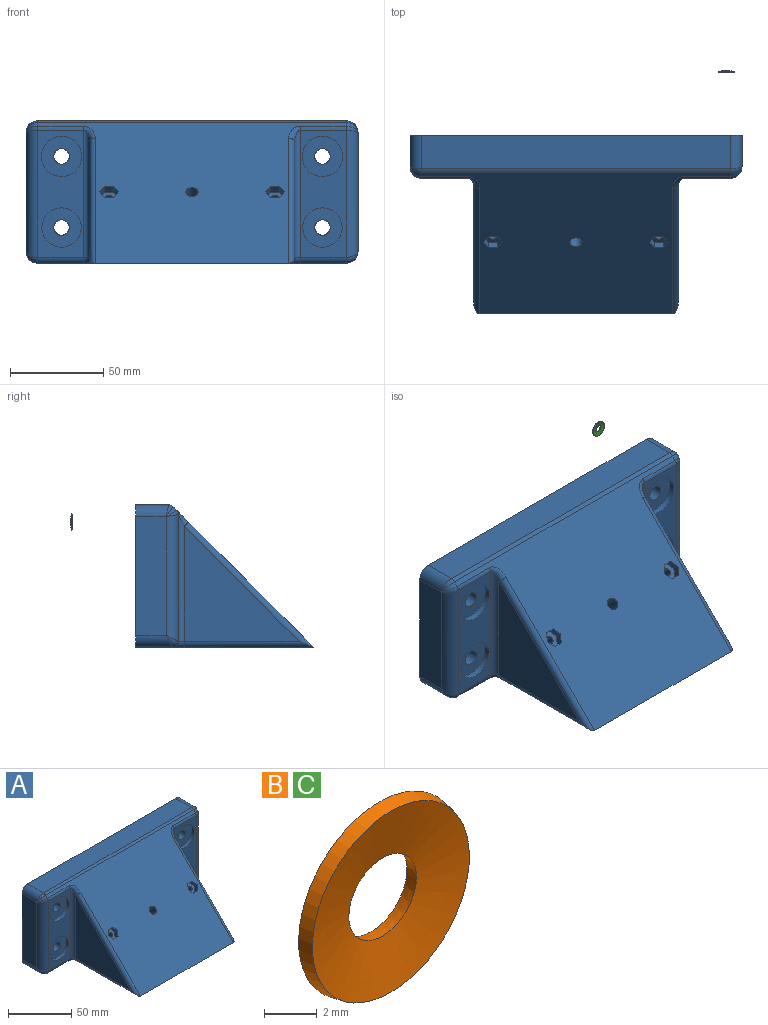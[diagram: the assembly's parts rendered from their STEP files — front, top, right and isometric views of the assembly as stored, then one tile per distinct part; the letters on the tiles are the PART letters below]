
ASSEMBLY  parts=3 mates=1
PART A: 74 faces, bbox 177.8x95.3x89.7 mm
  f0: cylinder r=4.13mm len=19.69mm, axis (0,1,0), area 510.5mm2, adj f10,f60
  f1: cylinder r=4.13mm len=19.69mm, axis (0,1,0), area 510.5mm2, adj f10,f63
  f2: cylinder r=4.13mm len=19.69mm, axis (0,1,0), area 510.5mm2, adj f10,f64
  f3: cylinder r=4.13mm len=19.69mm, axis (0,1,0), area 510.5mm2, adj f10,f67
  f4: plane 165.1x75.27mm, normal (0,-0.71,0.71), area 11064.4mm2, adj f7,f12,f21,f22,f23,f26,f28,f30
  f5: cylinder r=1.98mm len=9.26mm, axis (0,-0.71,0.71), area 113.8mm2, adj f39,f68
  f6: cylinder r=1.98mm len=9.26mm, axis (0,-0.71,0.71), area 113.8mm2, adj f38,f70
  f7: plane 165.1x95.25mm, normal (0,0,-1), area 10510.8mm2, adj f4,f10,f17,f18,f19,f24,f27,f29
  f8: plane 63.5x16.51mm, normal (1,0,0), area 1048.4mm2, adj f10,f53,f55,f57,f59
  f9: plane 63.5x16.51mm, normal (-1,0,0), area 1048.4mm2, adj f10,f46,f48,f50,f52
  f10: plane 177.8x76.2mm, normal (0,1,0), area 13299.7mm2, adj f0,f1,f2,f3,f7,f8,f9,f11
  f11: plane 165.1x17.74mm, normal (0,0,1), area 2928mm2, adj f10,f31,f46,f53
  f12: cylinder r=3.28mm len=17.54mm, axis (0,-0.71,0.71), area 375.9mm2, adj f4,f72
  f13: plane 67.9x24.38mm, normal (0,-1,0), area 939.9mm2, adj f24,f25,f26,f50,f65,f66
  f14: plane 61.55x61.55mm, normal (-1,0,0), area 1894.2mm2, adj f25,f29,f30
  f15: plane 61.55x61.55mm, normal (1,0,0), area 1894.2mm2, adj f19,f20,f21
  f16: plane 67.9x24.38mm, normal (0,-1,0), area 939.9mm2, adj f17,f20,f23,f57,f61,f62
  f17: cylinder r=3.17mm len=24.38mm, axis (-1,0,0), area 121.6mm2, adj f7,f16,f18,f58
  f18: torus R=6.35mm, axis (0,0,-1), area 33.9mm2, adj f7,f17,f19,f20
  f19: cylinder r=3.17mm len=69.22mm, axis (0,-1,0), area 331.3mm2, adj f7,f15,f18,f21
  f20: cylinder r=3.17mm len=67.9mm, axis (0,0,1), area 327.1mm2, adj f15,f16,f18,f22
  f21: cylinder r=3.17mm len=69.22mm, axis (0,-0.71,-0.71), area 458.5mm2, adj f4,f15,f19,f22
  f22: bspline ~9.7x7.45mm, area 35.1mm2, adj f4,f20,f21,f23
  f23: cylinder r=3.17mm len=24.38mm, axis (-1,0,0), area 60.8mm2, adj f4,f16,f22,f56
  f24: cylinder r=3.17mm len=24.38mm, axis (-1,0,0), area 121.6mm2, adj f7,f13,f27,f51
  f25: cylinder r=3.17mm len=67.9mm, axis (0,0,1), area 327.1mm2, adj f13,f14,f27,f28
  f26: cylinder r=3.17mm len=24.38mm, axis (-1,0,0), area 60.8mm2, adj f4,f13,f28,f49
  f27: torus R=6.35mm, axis (0,0,-1), area 33.9mm2, adj f7,f24,f25,f29
  f28: bspline ~9.7x7.45mm, area 35.1mm2, adj f4,f25,f26,f30
  f29: cylinder r=3.17mm len=69.22mm, axis (0,1,0), area 331.3mm2, adj f7,f14,f27,f30
  f30: cylinder r=3.17mm len=69.22mm, axis (0,0.71,0.71), area 458.5mm2, adj f4,f14,f28,f29
  f31: cylinder r=3.17mm len=165.1mm, axis (-1,0,0), area 411.7mm2, adj f4,f11,f47,f54
  f32: plane 4.99x3.09mm, normal (0,0.71,0.71), area 21.8mm2, adj f4,f33,f37,f38
  f33: plane 6.14x6.14mm, normal (-0.87,0.35,0.35), area 21.8mm2, adj f4,f32,f34,f38
  f34: plane 6.14x6.14mm, normal (-0.87,-0.35,-0.35), area 21.8mm2, adj f4,f33,f35,f38
  f35: plane 4.99x3.09mm, normal (0,-0.71,-0.71), area 21.8mm2, adj f4,f34,f36,f38
  f36: plane 6.14x6.14mm, normal (0.87,-0.35,-0.35), area 21.8mm2, adj f4,f35,f37,f38
  f37: plane 6.14x6.14mm, normal (0.87,0.35,0.35), area 21.8mm2, adj f4,f32,f36,f38
  f38: plane 9.97x6.11mm, normal (0,-0.71,0.71), area 52.2mm2, adj f6,f32,f33,f34,f35,f36,f37
  f39: plane 9.97x6.11mm, normal (0,-0.71,0.71), area 52.2mm2, adj f5,f40,f41,f42,f43,f44,f45
  f40: plane 6.14x6.14mm, normal (0.87,-0.35,-0.35), area 21.8mm2, adj f4,f39,f41,f45
  f41: plane 6.14x6.14mm, normal (0.87,0.35,0.35), area 21.8mm2, adj f4,f39,f40,f42
  f42: plane 4.99x3.09mm, normal (0,0.71,0.71), area 21.8mm2, adj f4,f39,f41,f43
  f43: plane 6.14x6.14mm, normal (-0.87,0.35,0.35), area 21.8mm2, adj f4,f39,f42,f44
  f44: plane 6.14x6.14mm, normal (-0.87,-0.35,-0.35), area 21.8mm2, adj f4,f39,f43,f45
  f45: plane 4.99x3.09mm, normal (0,-0.71,-0.71), area 21.8mm2, adj f4,f39,f40,f44
  f46: cylinder r=6.35mm len=17.74mm, axis (0,-1,0), area 172.1mm2, adj f9,f10,f11,f47
  f47: bspline ~7.25x6.35mm, area 16mm2, adj f31,f46,f48
  f48: cylinder r=6.35mm len=6.44mm, axis (0,-0.71,-0.71), area 18mm2, adj f4,f9,f47,f49
  f49: bspline ~7.25x6.35mm, area 16mm2, adj f26,f48,f50
  f50: cylinder r=6.35mm len=67.9mm, axis (0,0,-1), area 661mm2, adj f9,f13,f49,f51
  f51: bspline ~7.58x6.35mm, area 33.3mm2, adj f24,f50,f52
  f52: cylinder r=6.35mm len=19.69mm, axis (0,1,0), area 184.8mm2, adj f7,f9,f10,f51
  f53: cylinder r=6.35mm len=17.74mm, axis (0,1,0), area 172.1mm2, adj f8,f10,f11,f54
  f54: bspline ~7.25x6.35mm, area 16mm2, adj f31,f53,f55
  f55: cylinder r=6.35mm len=6.44mm, axis (0,0.71,0.71), area 18mm2, adj f4,f8,f54,f56
  f56: bspline ~6.58x6.35mm, area 16mm2, adj f23,f55,f57
  f57: cylinder r=6.35mm len=67.9mm, axis (0,0,-1), area 661mm2, adj f8,f16,f56,f58
  f58: bspline ~7.58x6.35mm, area 33.3mm2, adj f17,f57,f59
  f59: cylinder r=6.35mm len=19.69mm, axis (0,-1,0), area 184.8mm2, adj f7,f8,f10,f58
  f60: plane 21.59x21.59mm, normal (0,-1,0), area 312.6mm2, adj f0,f61
  f61: cylinder r=10.79mm len=21.59mm, axis (0,-1,0), area 215.4mm2, adj f16,f60
  f62: cylinder r=10.54mm len=21.08mm, axis (0,-1,0), area 210.3mm2, adj f16,f63
  f63: plane 21.08x21.08mm, normal (0,-1,0), area 295.5mm2, adj f1,f62
  f64: plane 21.08x21.08mm, normal (0,-1,0), area 295.5mm2, adj f2,f65
  f65: cylinder r=10.54mm len=21.08mm, axis (0,-1,0), area 210.3mm2, adj f13,f64
  f66: cylinder r=10.79mm len=21.59mm, axis (0,-1,0), area 215.4mm2, adj f13,f67
  f67: plane 21.59x21.59mm, normal (0,-1,0), area 312.6mm2, adj f3,f66
  f68: plane 9.14x6.47mm, normal (0,0.71,-0.71), area 53.3mm2, adj f5,f69
  f69: cylinder r=4.57mm len=38.26mm, axis (0,0.71,-0.71), area 1160.2mm2, adj f7,f68
  f70: plane 9.14x6.47mm, normal (0,0.71,-0.71), area 53.3mm2, adj f6,f71
  f71: cylinder r=4.57mm len=38.26mm, axis (0,0.71,-0.71), area 1160.2mm2, adj f7,f70
  f72: plane 19.05x13.47mm, normal (0,0.71,-0.71), area 251.3mm2, adj f12,f73
  f73: cylinder r=9.53mm len=45.4mm, axis (0,0.71,-0.71), area 2132.1mm2, adj f7,f72
PART B: 4 faces, bbox 8.7x1.1x8.7 mm
  f0: cone r=1.82mm half-angle=79.6deg, axis (0,-1,0), area 46.2mm2, adj f1,f3
  f1: cone r=1.93mm half-angle=10.4deg, axis (0,1,0), area 7.5mm2, adj f0,f2
  f2: cone r=4.33mm half-angle=79.6deg, axis (0,-1,0), area 48mm2, adj f1,f3
  f3: cone r=4.22mm half-angle=10.4deg, axis (0,1,0), area 17mm2, adj f0,f2
PART C: same geometry as B
PLACE A t=(-79.65,42.8,-29.2)mm
PLACE B rot(axis=(-1,0,0),45deg) t=(53.7,-4.07,-1.37)mm
PLACE C t=(89.77,76.53,37.85)mm
MATE cylindrical B.f0 <-> A.f69  axis (0,-0.71,0.71) through (53.7,-3.32,-2.13)mm
